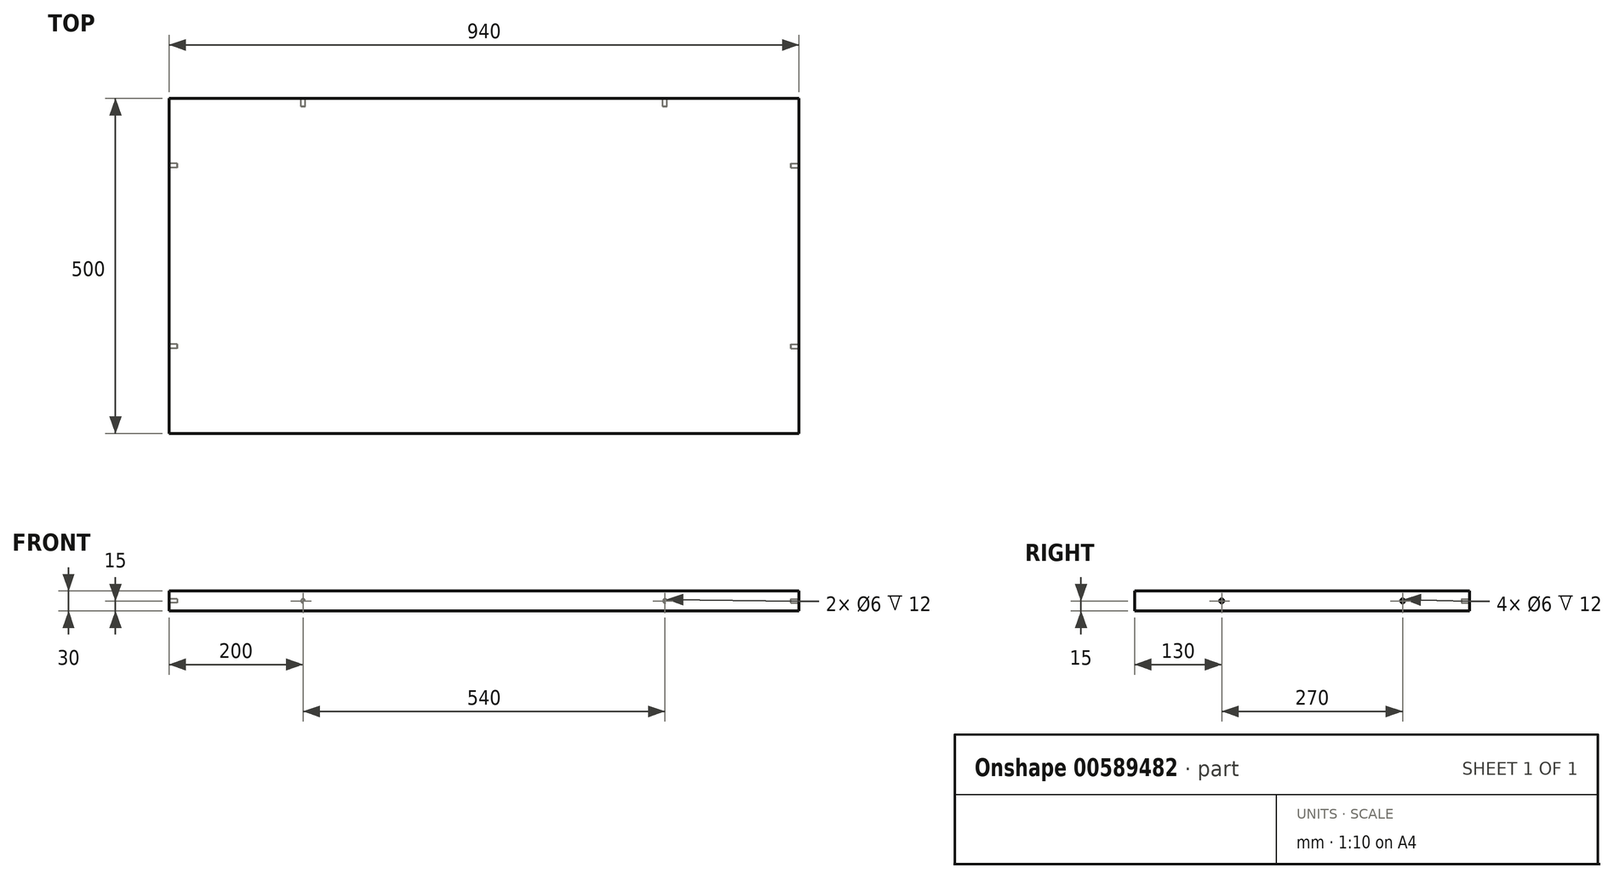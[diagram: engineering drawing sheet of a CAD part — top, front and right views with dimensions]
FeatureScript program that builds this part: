
annotation { "Feature Type Name" : "Feature", "Feature Type Description" : "" }
export const myFeature = defineFeature(function(context is Context, id is Id, definition is map)
    precondition{}
    {
        {
            var Q0;
            Q0=qCreatedBy(makeId("Top.planeOp"),FACE);
            var sketch = newSketch(context, id + "F0", { "sketchPlane" : qUnion([Q0])});
            skLineSegment(sketch, "E0.bottom", {"start": v(0, 0) * mm, "end": v(940, 0) * mm});
            skLineSegment(sketch, "E0.top", {"start": v(0, 500) * mm, "end": v(940, 500) * mm});
            skLineSegment(sketch, "E0.left", {"start": v(0, 0) * mm, "end": v(0, 500) * mm});
            skLineSegment(sketch, "E0.right", {"start": v(940, 0) * mm, "end": v(940, 500) * mm});
            skSolve(sketch);
        }
        {
            var Q0;
            Q0=makeQuery(id+"F0.imprint","IMPRINT",FACE,{"disambiguationData":[TD([[makeQuery(id+"F0.imprint","IMPRINT",EDGE,{"derivedFrom":sQuery(id+"F0.wireOp",EDGE,"E0.bottom")}),1.0]])]});
            extrude(context, id + "F1", {"entities" : qUnion([Q0]), "depth" : 30 * mm, "offsetDistance" : 25 * mm});
        }
        {
            var Q0;
            Q0=makeQuery(id+"F1.opExtrude","SWEPT_FACE",FACE,{"disambiguationData":[OSD([sQuery(id+"F0.wireOp",EDGE,"E0.right")])]});
            var sketch = newSketch(context, id + "F2", { "sketchPlane" : qUnion([Q0])});
            skCircle(sketch, "E1", {"center": v(130, 15) * mm, "radius": 3 * mm});
            skPoint(sketch, "E1.centerSnap0", {"position": v(0, 15) * mm});
            skSolve(sketch);
        }
        {
            var Q0;
            Q0=makeQuery(id+"F2.imprint","IMPRINT",FACE,{"disambiguationData":[TD([[makeQuery(id+"F2.imprint","IMPRINT",EDGE,{"derivedFrom":sQuery(id+"F2.wireOp",EDGE,"E1")}),1.0]])]});
            extrude(context, id + "F3", {"entities" : qUnion([Q0]), "operationType" : NewBodyOperationType.REMOVE, "oppositeDirection" : true, "depth" : 12 * mm, "offsetDistance" : 25 * mm});
        }
        {
            var Q0;
            Q0=makeQuery(id+"F1.opExtrude","SWEPT_FACE",FACE,{"disambiguationData":[OSD([sQuery(id+"F0.wireOp",EDGE,"E0.right")])]});
            var sketch = newSketch(context, id + "F4", { "sketchPlane" : qUnion([Q0])});
            skCircle(sketch, "E2", {"center": v(400, 15) * mm, "radius": 3 * mm});
            skPoint(sketch, "E2.centerSnap0", {"position": v(500, 15) * mm});
            skSolve(sketch);
        }
        {
            var Q0;
            Q0=makeQuery(id+"F4.imprint","IMPRINT",FACE,{"disambiguationData":[TD([[makeQuery(id+"F4.imprint","IMPRINT",EDGE,{"derivedFrom":sQuery(id+"F4.wireOp",EDGE,"E2")}),1.0]])]});
            extrude(context, id + "F5", {"entities" : qUnion([Q0]), "operationType" : NewBodyOperationType.REMOVE, "oppositeDirection" : true, "depth" : 12 * mm, "offsetDistance" : 25 * mm});
        }
        {
            var Q0;
            Q0=makeQuery(id+"F1.opExtrude","SWEPT_FACE",FACE,{"disambiguationData":[OSD([sQuery(id+"F0.wireOp",EDGE,"E0.left")])]});
            var sketch = newSketch(context, id + "F6", { "sketchPlane" : qUnion([Q0])});
            skCircle(sketch, "E3.0", {"center": v(-400, 15) * mm, "radius": 3 * mm});
            skSolve(sketch);
        }
        {
            var Q0;
            Q0=makeQuery(id+"F6.imprint","IMPRINT",FACE,{"disambiguationData":[TD([[makeQuery(id+"F6.imprint","IMPRINT",EDGE,{"derivedFrom":sQuery(id+"F6.wireOp",EDGE,"E3.0")}),1.0]])]});
            extrude(context, id + "F7", {"entities" : qUnion([Q0]), "operationType" : NewBodyOperationType.REMOVE, "oppositeDirection" : true, "depth" : 12 * mm, "offsetDistance" : 25 * mm});
        }
        {
            var Q0;
            Q0=makeQuery(id+"F1.opExtrude","SWEPT_FACE",FACE,{"disambiguationData":[OSD([sQuery(id+"F0.wireOp",EDGE,"E0.left")])]});
            var sketch = newSketch(context, id + "F8", { "sketchPlane" : qUnion([Q0])});
            skCircle(sketch, "E4.0", {"center": v(-130, 15) * mm, "radius": 3 * mm});
            skSolve(sketch);
        }
        {
            var Q0;
            Q0=makeQuery(id+"F8.imprint","IMPRINT",FACE,{"disambiguationData":[TD([[makeQuery(id+"F8.imprint","IMPRINT",EDGE,{"derivedFrom":sQuery(id+"F8.wireOp",EDGE,"E4.0")}),1.0]])]});
            extrude(context, id + "F9", {"entities" : qUnion([Q0]), "operationType" : NewBodyOperationType.REMOVE, "oppositeDirection" : true, "depth" : 12 * mm, "offsetDistance" : 25 * mm});
        }
        {
            var Q0;
            Q0=makeQuery(id+"F1.opExtrude","SWEPT_FACE",FACE,{"disambiguationData":[OSD([sQuery(id+"F0.wireOp",EDGE,"E0.top")])]});
            var sketch = newSketch(context, id + "F10", { "sketchPlane" : qUnion([Q0])});
            skCircle(sketch, "E5", {"center": v(-740, 15) * mm, "radius": 3 * mm});
            skPoint(sketch, "E5.centerSnap0", {"position": v(-940, 15) * mm});
            skCircle(sketch, "E6", {"center": v(-200, 15) * mm, "radius": 3 * mm});
            skPoint(sketch, "E6.centerSnap0", {"position": v(0, 15) * mm});
            skSolve(sketch);
        }
        {
            var Q0;
            Q0=makeQuery(id+"F10.imprint","IMPRINT",FACE,{"disambiguationData":[TD([[makeQuery(id+"F10.imprint","IMPRINT",EDGE,{"derivedFrom":sQuery(id+"F10.wireOp",EDGE,"E5")}),1.0]])]});
            var Q1;
            Q1=makeQuery(id+"F10.imprint","IMPRINT",FACE,{"disambiguationData":[TD([[makeQuery(id+"F10.imprint","IMPRINT",EDGE,{"derivedFrom":sQuery(id+"F10.wireOp",EDGE,"E6")}),1.0]])]});
            extrude(context, id + "F11", {"entities" : qUnion([Q0, Q1]), "operationType" : NewBodyOperationType.REMOVE, "oppositeDirection" : true, "depth" : 12 * mm, "offsetDistance" : 25 * mm});
        }
    });
